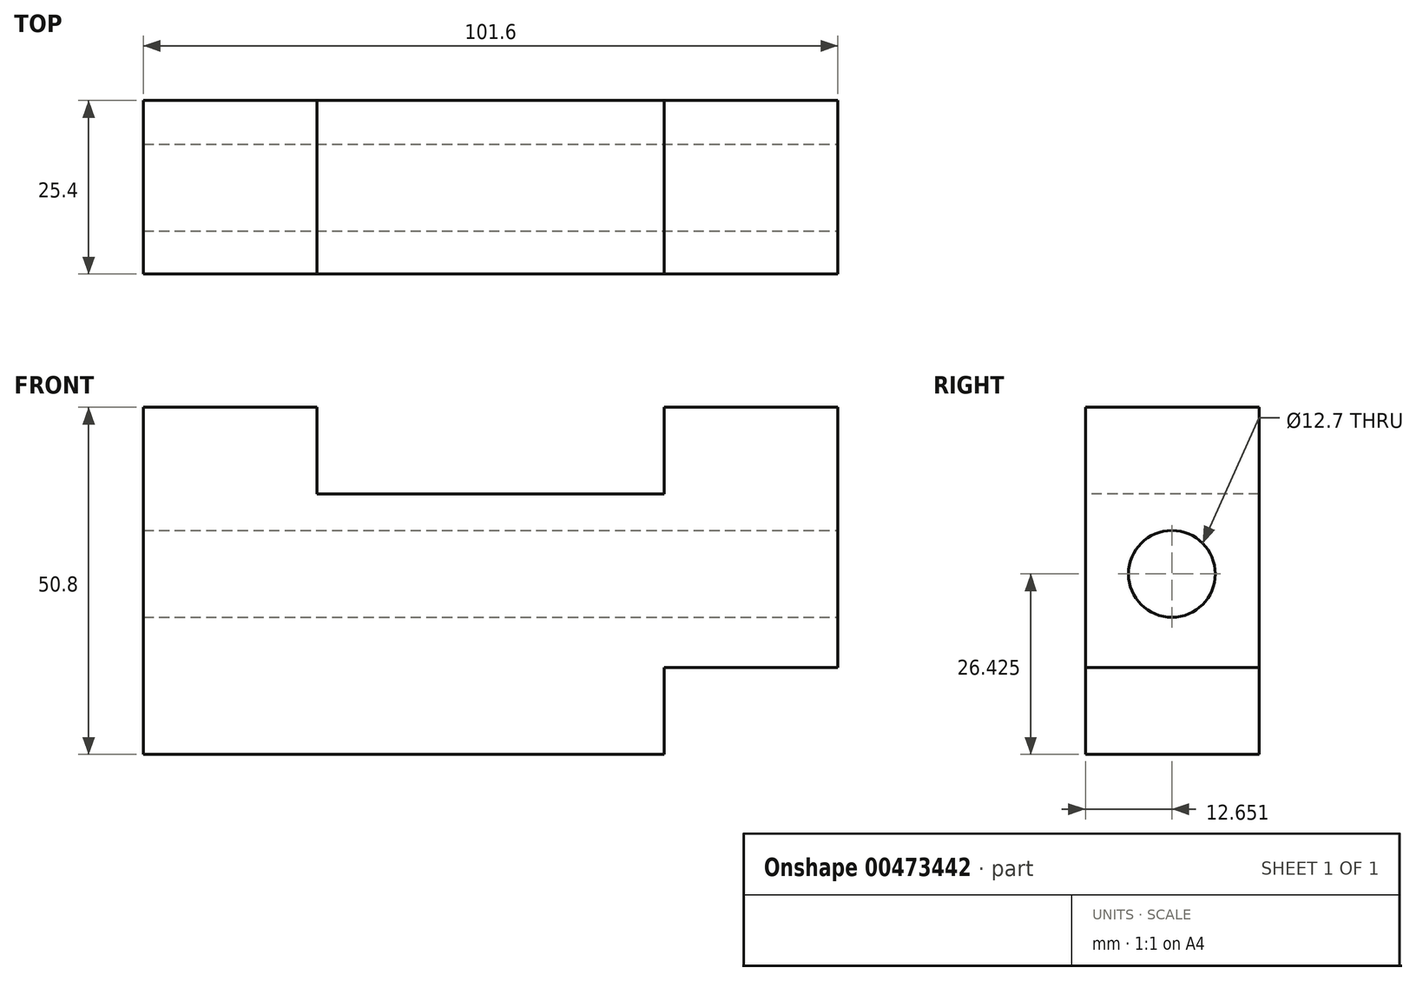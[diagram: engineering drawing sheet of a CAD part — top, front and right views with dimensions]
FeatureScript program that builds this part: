
annotation { "Feature Type Name" : "Feature", "Feature Type Description" : "" }
export const myFeature = defineFeature(function(context is Context, id is Id, definition is map)
    precondition{}
    {
        {
            var Q0;
            Q0=qCreatedBy(makeId("Front.planeOp"),FACE);
            var sketch = newSketch(context, id + "F0", { "sketchPlane" : qUnion([Q0])});
            skLineSegment(sketch, "E0.bottom", {"start": v(-50.8, 25.4) * mm, "end": v(50.8, 25.4) * mm});
            skLineSegment(sketch, "E0.top", {"start": v(-50.8, -25.4) * mm, "end": v(50.8, -25.4) * mm});
            skLineSegment(sketch, "E0.left", {"start": v(-50.8, 25.4) * mm, "end": v(-50.8, -25.4) * mm});
            skLineSegment(sketch, "E0.right", {"start": v(50.8, 25.4) * mm, "end": v(50.8, -25.4) * mm});
            skPoint(sketch, "E0.middle", {"position": v(0, 0) * mm});
            skSolve(sketch);
        }
        {
            var Q0;
            Q0 = qSketchRegion(id + "F0", true);
            extrude(context, id + "F1", {"entities" : qUnion([Q0]), "depth" : 25.4 * mm});
        }
        {
            var Q0;
            Q0=makeQuery(id+"F1.opExtrude","CAP_FACE",FACE,{"disambiguationData":[OSD([sQuery(id+"F0.wireOp",EDGE,"E0.bottom"),sQuery(id+"F0.wireOp",EDGE,"E0.top"),sQuery(id+"F0.wireOp",EDGE,"E0.left"),sQuery(id+"F0.wireOp",EDGE,"E0.right")])],"isStart":false});
            var sketch = newSketch(context, id + "F2", { "sketchPlane" : qUnion([Q0])});
            skLineSegment(sketch, "E1.bottom", {"start": v(50.8, -12.7) * mm, "end": v(25.4, -12.7) * mm});
            skLineSegment(sketch, "E1.top", {"start": v(50.8, -25.4) * mm, "end": v(25.4, -25.4) * mm});
            skLineSegment(sketch, "E1.left", {"start": v(50.8, -12.7) * mm, "end": v(50.8, -25.4) * mm});
            skLineSegment(sketch, "E1.right", {"start": v(25.4, -12.7) * mm, "end": v(25.4, -25.4) * mm});
            skSolve(sketch);
        }
        {
            var Q0;
            Q0 = qSketchRegion(id + "F2", true);
            extrude(context, id + "F3", {"entities" : qUnion([Q0]), "operationType" : NewBodyOperationType.REMOVE, "endBound" : BoundingType.THROUGH_ALL, "oppositeDirection" : true, "depth" : 25.4 * mm});
        }
        {
            var Q0;
            Q0=makeQuery(id+"F1.opExtrude","SWEPT_FACE",FACE,{"disambiguationData":[OSD([sQuery(id+"F0.wireOp",EDGE,"E0.right")])]});
            var sketch = newSketch(context, id + "F4", { "sketchPlane" : qUnion([Q0])});
            skCircle(sketch, "E2", {"center": v(-12.75, 1.02) * mm, "radius": 6.35 * mm});
            skSolve(sketch);
        }
        {
            var Q0;
            Q0 = qSketchRegion(id + "F4", true);
            extrude(context, id + "F5", {"entities" : qUnion([Q0]), "operationType" : NewBodyOperationType.REMOVE, "endBound" : BoundingType.THROUGH_ALL, "oppositeDirection" : true, "depth" : 25.4 * mm});
        }
        {
            var Q0;
            Q0=makeQuery(id+"F1.opExtrude","CAP_FACE",FACE,{"disambiguationData":[OSD([sQuery(id+"F0.wireOp",EDGE,"E0.bottom"),sQuery(id+"F0.wireOp",EDGE,"E0.top"),sQuery(id+"F0.wireOp",EDGE,"E0.left"),sQuery(id+"F0.wireOp",EDGE,"E0.right")])],"isStart":false});
            var sketch = newSketch(context, id + "F6", { "sketchPlane" : qUnion([Q0])});
            skLineSegment(sketch, "E3.bottom", {"start": v(-25.4, 25.4) * mm, "end": v(25.4, 25.4) * mm});
            skLineSegment(sketch, "E3.top", {"start": v(-25.4, 12.7) * mm, "end": v(25.4, 12.7) * mm});
            skLineSegment(sketch, "E3.left", {"start": v(-25.4, 25.4) * mm, "end": v(-25.4, 12.7) * mm});
            skLineSegment(sketch, "E3.right", {"start": v(25.4, 25.4) * mm, "end": v(25.4, 12.7) * mm});
            skSolve(sketch);
        }
        {
            var Q0;
            Q0 = qSketchRegion(id + "F6", true);
            extrude(context, id + "F7", {"entities" : qUnion([Q0]), "operationType" : NewBodyOperationType.REMOVE, "endBound" : BoundingType.THROUGH_ALL, "oppositeDirection" : true, "depth" : 25.4 * mm});
        }
    });
